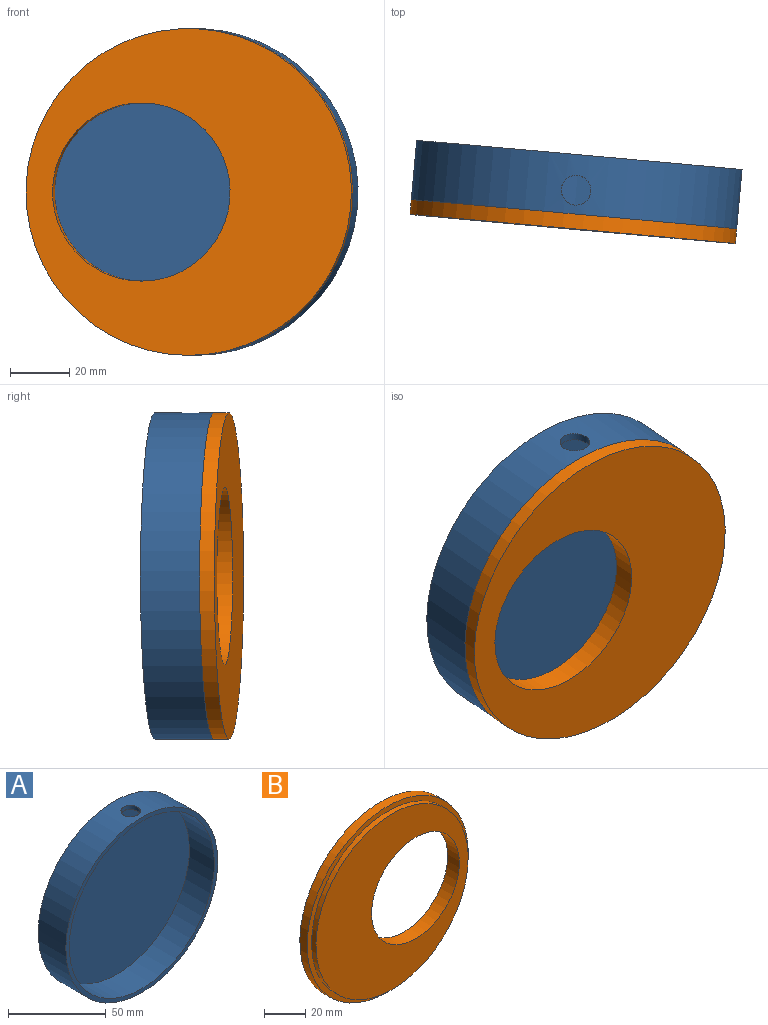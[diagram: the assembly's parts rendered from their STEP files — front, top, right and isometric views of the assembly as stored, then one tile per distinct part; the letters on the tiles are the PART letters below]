
ASSEMBLY  parts=2 mates=1
PART A: 6 faces, bbox 110x20x110 mm
  f0: cylinder r=55mm len=110mm, axis (0,1,0), area 6832.9mm2, adj f2,f3,f5
  f1: cylinder r=52.5mm len=105mm, axis (0,-1,0), area 5858.8mm2, adj f2,f4,f5
  f2: plane 110x110mm, normal (0,-1,0), area 844.3mm2, adj f0,f1
  f3: plane 110x110mm, normal (0,1,0), area 9503.3mm2, adj f0
  f4: plane 105x105mm, normal (0,-1,0), area 8659mm2, adj f1
  f5: cylinder r=5mm len=10mm, axis (0,0,-1), area 78.7mm2, adj f0,f1
PART B: 6 faces, bbox 110x8x110 mm
  f0: cylinder r=55mm len=110mm, axis (0,1,0), area 1727.9mm2, adj f1,f2
  f1: plane 110x110mm, normal (0,-1,0), area 1008.5mm2, adj f0,f3
  f2: plane 110x110mm, normal (0,1,0), area 6675.9mm2, adj f0,f5
  f3: cylinder r=52mm len=104mm, axis (0,1,0), area 980.2mm2, adj f1,f4
  f4: plane 104x104mm, normal (0,-1,0), area 5667.4mm2, adj f3,f5
  f5: cylinder r=30mm len=60mm, axis (0,-1,0), area 1508mm2, adj f2,f4
PLACE A rot(axis=(0,0,-1),5.1deg) t=(-15.3,-92.56,12.7)mm
PLACE B rot(axis=(0,0,1),174.9deg) t=(142.52,-131.8,12.7)mm
MATE slider A.f1 <-> B.f0  axis (-0.09,-1,0) through (-17.09,-112.48,12.7)mm
